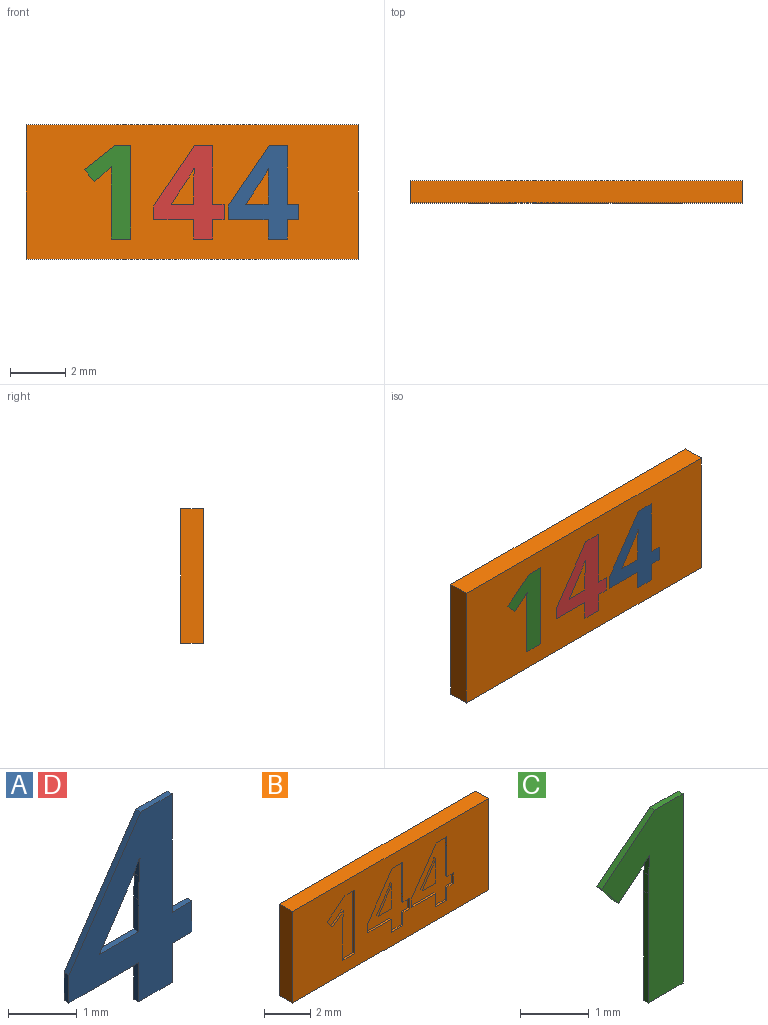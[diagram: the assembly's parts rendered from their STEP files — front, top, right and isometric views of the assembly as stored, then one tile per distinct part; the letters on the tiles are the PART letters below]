
ASSEMBLY  parts=4 mates=3
PART A: 20 faces, bbox 2.5x0.1x3.4 mm
  f0: plane 3.37x2.54mm, normal (0,-1,0), area 4.3mm2, adj f1,f2,f3,f4,f5,f6,f7,f8
  f1: plane 0.41x0.1mm, normal (0,0,1), area 0mm2, adj f0,f2,f13,f15
  f2: plane 2.12x0.1mm, normal (1,0,0), area 0.2mm2, adj f0,f1,f3,f13
  f3: plane 0.66x0.1mm, normal (0,0,1), area 0.1mm2, adj f0,f2,f4,f13
  f4: plane 2.18x1.48mm, normal (-0.83,0,0.56), area 0.3mm2, adj f0,f3,f5,f13
  f5: plane 0.5x0.1mm, normal (-1,0,0), area 0mm2, adj f0,f4,f6,f13
  f6: plane 1.44x0.1mm, normal (0,0,-1), area 0.1mm2, adj f0,f5,f7,f13
  f7: plane 0.7x0.1mm, normal (-1,0,0), area 0.1mm2, adj f0,f6,f8,f13
  f8: plane 0.7x0.1mm, normal (0,0,-1), area 0.1mm2, adj f0,f7,f13,f14
  f9: plane 0.93x0.62mm, normal (0.83,0,-0.55), area 0.1mm2, adj f0,f10,f13,f18
  f10: extruded ~0.37x0.21mm, area 0mm2, adj f0,f9,f11,f13
  f11: plane 0.1x0.02mm, normal (0,0,-1), area 0mm2, adj f0,f10,f12,f13
  f12: extruded ~0.32x0.1mm, area 0mm2, adj f0,f11,f13,f17
  f13: plane 3.37x2.54mm, normal (0,1,0), area 4.3mm2, adj f1,f2,f3,f4,f5,f6,f7,f8
  f14: plane 0.7x0.1mm, normal (1,0,0), area 0.1mm2, adj f0,f8,f13,f16
  f15: plane 0.55x0.1mm, normal (1,0,0), area 0.1mm2, adj f0,f1,f13,f16
  f16: plane 0.41x0.1mm, normal (0,0,-1), area 0mm2, adj f0,f13,f14,f15
  f17: extruded ~0.42x0.1mm, area 0mm2, adj f0,f12,f13,f19
  f18: plane 0.81x0.1mm, normal (0,0,1), area 0.1mm2, adj f0,f9,f13,f19
  f19: plane 0.57x0.1mm, normal (-1,0,0), area 0.1mm2, adj f0,f13,f17,f18
PART B: 57 faces, bbox 12x0.8x4.9 mm
  f0: plane 12x4.85mm, normal (0,-1,0), area 45.6mm2, adj f1,f2,f3,f4,f6,f7,f8,f9
  f1: plane 12x0.8mm, normal (0,0,-1), area 9.6mm2, adj f0,f2,f4,f5
  f2: plane 4.85x0.8mm, normal (1,0,0), area 3.9mm2, adj f0,f1,f3,f5
  f3: plane 12x0.8mm, normal (0,0,1), area 9.6mm2, adj f0,f2,f4,f5
  f4: plane 4.85x0.8mm, normal (-1,0,0), area 3.9mm2, adj f0,f1,f3,f5
  f5: plane 12x4.85mm, normal (0,1,0), area 58.2mm2, adj f1,f2,f3,f4
  f6: plane 0.55x0.1mm, normal (-1,0,0), area 0.1mm2, adj f0,f7,f23,f24
  f7: plane 0.41x0.1mm, normal (0,0,-1), area 0mm2, adj f0,f6,f8,f24
  f8: plane 2.12x0.1mm, normal (-1,0,0), area 0.2mm2, adj f0,f7,f9,f24
  f9: plane 0.66x0.1mm, normal (0,0,-1), area 0.1mm2, adj f0,f8,f10,f24
  f10: plane 2.18x1.48mm, normal (0.83,0,-0.56), area 0.3mm2, adj f0,f9,f11,f24
  f11: plane 0.5x0.1mm, normal (1,0,0), area 0mm2, adj f0,f10,f12,f24
  f12: plane 1.44x0.1mm, normal (0,0,1), area 0.1mm2, adj f0,f11,f13,f24
  f13: plane 0.7x0.1mm, normal (1,0,0), area 0.1mm2, adj f0,f12,f14,f24
  f14: plane 0.7x0.1mm, normal (0,0,1), area 0.1mm2, adj f0,f13,f15,f24
  f15: plane 0.7x0.1mm, normal (-1,0,0), area 0.1mm2, adj f0,f14,f23,f24
  f16: plane 0.81x0.1mm, normal (0,0,-1), area 0.1mm2, adj f17,f22,f24,f25
  f17: plane 0.93x0.62mm, normal (-0.83,0,0.55), area 0.1mm2, adj f16,f18,f24,f25
  f18: extruded ~0.37x0.21mm, area 0mm2, adj f17,f19,f24,f25
  f19: plane 0.1x0.02mm, normal (0,0,1), area 0mm2, adj f18,f20,f24,f25
  f20: extruded ~0.32x0.1mm, area 0mm2, adj f19,f21,f24,f25
  f21: extruded ~0.42x0.1mm, area 0mm2, adj f20,f22,f24,f25
  f22: plane 0.57x0.1mm, normal (1,0,0), area 0.1mm2, adj f16,f21,f24,f25
  f23: plane 0.41x0.1mm, normal (0,0,1), area 0mm2, adj f0,f6,f15,f24
  f24: plane 3.37x2.54mm, normal (0,-1,0), area 4.3mm2, adj f6,f7,f8,f9,f10,f11,f12,f13
  f25: plane 1.3x0.84mm, normal (0,-1,0), area 0.5mm2, adj f16,f17,f18,f19,f20,f21,f22
  f26: plane 0.55x0.1mm, normal (-1,0,0), area 0.1mm2, adj f0,f27,f43,f44
  f27: plane 0.41x0.1mm, normal (0,0,-1), area 0mm2, adj f0,f26,f28,f44
  f28: plane 2.12x0.1mm, normal (-1,0,0), area 0.2mm2, adj f0,f27,f29,f44
  f29: plane 0.66x0.1mm, normal (0,0,-1), area 0.1mm2, adj f0,f28,f30,f44
  f30: plane 2.18x1.48mm, normal (0.83,0,-0.56), area 0.3mm2, adj f0,f29,f31,f44
  f31: plane 0.5x0.1mm, normal (1,0,0), area 0mm2, adj f0,f30,f32,f44
  f32: plane 1.44x0.1mm, normal (0,0,1), area 0.1mm2, adj f0,f31,f33,f44
  f33: plane 0.7x0.1mm, normal (1,0,0), area 0.1mm2, adj f0,f32,f34,f44
  f34: plane 0.7x0.1mm, normal (0,0,1), area 0.1mm2, adj f0,f33,f35,f44
  f35: plane 0.7x0.1mm, normal (-1,0,0), area 0.1mm2, adj f0,f34,f43,f44
  f36: plane 0.81x0.1mm, normal (0,0,-1), area 0.1mm2, adj f37,f42,f44,f45
  f37: plane 0.93x0.62mm, normal (-0.83,0,0.55), area 0.1mm2, adj f36,f38,f44,f45
  f38: extruded ~0.37x0.21mm, area 0mm2, adj f37,f39,f44,f45
  f39: plane 0.1x0.02mm, normal (0,0,1), area 0mm2, adj f38,f40,f44,f45
  f40: extruded ~0.32x0.1mm, area 0mm2, adj f39,f41,f44,f45
  f41: extruded ~0.42x0.1mm, area 0mm2, adj f40,f42,f44,f45
  f42: plane 0.57x0.1mm, normal (1,0,0), area 0.1mm2, adj f36,f41,f44,f45
  f43: plane 0.41x0.1mm, normal (0,0,1), area 0mm2, adj f0,f26,f35,f44
  f44: plane 3.37x2.54mm, normal (0,-1,0), area 4.3mm2, adj f26,f27,f28,f29,f30,f31,f32,f33
  f45: plane 1.3x0.84mm, normal (0,-1,0), area 0.5mm2, adj f36,f37,f38,f39,f40,f41,f42
  f46: plane 3.37x0.1mm, normal (-1,0,0), area 0.3mm2, adj f0,f47,f55,f56
  f47: plane 0.59x0.1mm, normal (0,0,-1), area 0.1mm2, adj f0,f46,f48,f56
  f48: plane 1.09x0.86mm, normal (0.62,0,-0.78), area 0.1mm2, adj f0,f47,f49,f56
  f49: plane 0.43x0.34mm, normal (0.78,0,0.63), area 0.1mm2, adj f0,f48,f50,f56
  f50: plane 0.39x0.31mm, normal (-0.63,0,0.78), area 0mm2, adj f0,f49,f51,f56
  f51: extruded ~0.25x0.23mm, area 0mm2, adj f0,f50,f52,f56
  f52: plane 0.35x0.1mm, normal (1,0,-0.03), area 0mm2, adj f0,f51,f53,f56
  f53: plane 0.32x0.1mm, normal (1,0,-0.02), area 0mm2, adj f0,f52,f54,f56
  f54: plane 1.95x0.1mm, normal (1,0,0), area 0.2mm2, adj f0,f53,f55,f56
  f55: plane 0.71x0.1mm, normal (0,0,1), area 0.1mm2, adj f0,f46,f54,f56
  f56: plane 3.37x1.67mm, normal (0,-1,0), area 2.9mm2, adj f46,f47,f48,f49,f50,f51,f52,f53
PART C: 12 faces, bbox 1.7x0.1x3.4 mm
  f0: plane 3.37x1.67mm, normal (0,-1,0), area 2.9mm2, adj f1,f2,f3,f4,f5,f6,f7,f9
  f1: plane 0.59x0.1mm, normal (0,0,1), area 0.1mm2, adj f0,f2,f8,f10
  f2: plane 1.09x0.86mm, normal (-0.62,0,0.78), area 0.1mm2, adj f0,f1,f3,f8
  f3: plane 0.43x0.34mm, normal (-0.78,0,-0.63), area 0.1mm2, adj f0,f2,f4,f8
  f4: plane 0.39x0.31mm, normal (0.63,0,-0.78), area 0mm2, adj f0,f3,f5,f8
  f5: extruded ~0.25x0.23mm, area 0mm2, adj f0,f4,f6,f8
  f6: plane 0.35x0.1mm, normal (-1,0,0.03), area 0mm2, adj f0,f5,f7,f8
  f7: plane 0.32x0.1mm, normal (-1,0,0.02), area 0mm2, adj f0,f6,f8,f9
  f8: plane 3.37x1.67mm, normal (0,1,0), area 2.9mm2, adj f1,f2,f3,f4,f5,f6,f7,f9
  f9: plane 1.95x0.1mm, normal (-1,0,0), area 0.2mm2, adj f0,f7,f8,f11
  f10: plane 3.37x0.1mm, normal (1,0,0), area 0.3mm2, adj f0,f1,f8,f11
  f11: plane 0.71x0.1mm, normal (0,0,-1), area 0.1mm2, adj f0,f8,f9,f10
PART D: same geometry as A
PLACE A t=(1.14,0.38,-0.04)mm
PLACE B t=(0.01,0.38,-0.04)mm
PLACE C t=(-4.58,0.38,-0.04)mm
PLACE D t=(-1.55,0.38,-0.04)mm
MATE fastened C.f0 <-> B.f0  axis (0,-1,0) through (-2.91,-0.42,-1.74)mm
MATE fastened A.f0 <-> B.f0  axis (0,-1,0) through (2.76,-0.42,-1.74)mm
MATE fastened D.f0 <-> B.f0  axis (0,-1,0) through (0.07,-0.42,-1.74)mm
